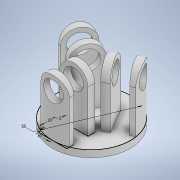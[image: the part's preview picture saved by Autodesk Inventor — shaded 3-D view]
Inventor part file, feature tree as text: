
AUTODESK INVENTOR PART (.ipt)
format: ipt  version: 2022 (Build 260153000, 153)  size: 208,896 bytes
history: native  units: mm
features: extrude x3, sketch x2, pattern_circular x1
ambient origin geometry x8: Origin, YZ Plane, XZ Plane, XY Plane, X Axis, Y Axis, Z Axis, Center Point
bodies: Solid1 (feature_tree)
feature tree (6):
  sketch  "Sketch1"  dims[d0=55.0mm d1=5.0mm]
  extrude  "Extrusion1"  Depth=5.0mm
  extrude  "Extrusion2"  Depth=10.0mm
  extrude  "Extrusion3"  Depth=10.0mm
  pattern_circular  "Circular Pattern1"  Count=4  [1 undecoded]
  sketch  "Sketch2"  dims[d2=5.0mm d3=10.0mm d4=10.0mm d5=40.0mm d6=0.0mm d7=5.0mm d8=0.0mm d9=30.0mm d10=360.0deg d12=14.0mm d13=20.0mm d14=0.0mm d15=5.0mm d16=0.0mm]
note: 1 required parameter value undecoded (feature->parameter linkage not recoverable at this tier; creation-order binding heuristic only, values carry confidence <= 0.55)
